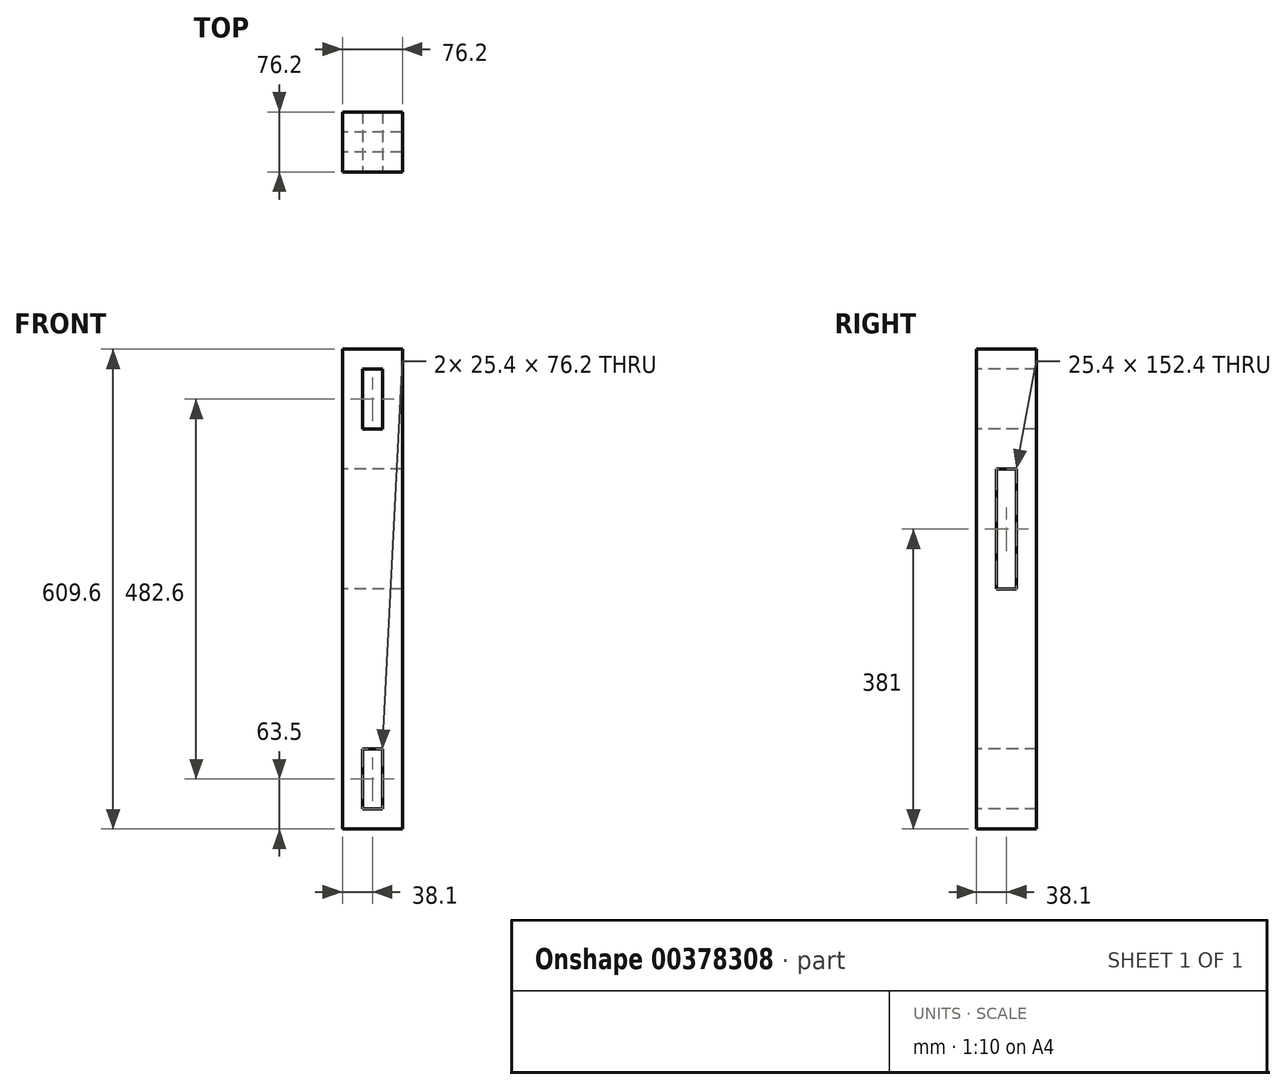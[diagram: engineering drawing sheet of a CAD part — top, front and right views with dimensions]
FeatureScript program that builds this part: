
annotation { "Feature Type Name" : "Feature", "Feature Type Description" : "" }
export const myFeature = defineFeature(function(context is Context, id is Id, definition is map)
    precondition{}
    {
        {
            var Q0;
            Q0=qCreatedBy(makeId("Right.planeOp"),FACE);
            var sketch = newSketch(context, id + "F0", { "sketchPlane" : qUnion([Q0])});
            skLineSegment(sketch, "E0.bottom", {"start": v(-12.7, -88.9) * mm, "end": v(12.7, -88.9) * mm});
            skLineSegment(sketch, "E0.top", {"start": v(-12.7, -241.3) * mm, "end": v(12.7, -241.3) * mm});
            skLineSegment(sketch, "E0.left", {"start": v(-12.7, -88.9) * mm, "end": v(-12.7, -241.3) * mm});
            skLineSegment(sketch, "E0.right", {"start": v(12.7, -88.9) * mm, "end": v(12.7, -241.3) * mm});
            skLineSegment(sketch, "E1.bottom", {"start": v(-38.1, 63.5) * mm, "end": v(38.1, 63.5) * mm});
            skLineSegment(sketch, "E1.top", {"start": v(-38.1, -546.1) * mm, "end": v(38.1, -546.1) * mm});
            skLineSegment(sketch, "E1.left", {"start": v(-38.1, 63.5) * mm, "end": v(-38.1, -546.1) * mm});
            skLineSegment(sketch, "E1.right", {"start": v(38.1, 63.5) * mm, "end": v(38.1, -546.1) * mm});
            skSolve(sketch);
        }
        {
            var Q0;
            Q0 = qSketchRegion(id + "F0", true);
            extrude(context, id + "F1", {"entities" : qUnion([Q0]), "depth" : 38.1 * mm, "hasSecondDirection" : true, "secondDirectionOppositeDirection" : true, "secondDirectionDepth" : 38.1 * mm});
        }
        {
            var Q0;
            Q0=makeQuery(id+"F1.opExtrude","SWEPT_FACE",FACE,{"disambiguationData":[OSD([sQuery(id+"F0.wireOp",EDGE,"E1.left")])]});
            var sketch = newSketch(context, id + "F2", { "sketchPlane" : qUnion([Q0])});
            skLineSegment(sketch, "E2.bottom", {"start": v(-12.7, 38.1) * mm, "end": v(12.7, 38.1) * mm});
            skLineSegment(sketch, "E2.top", {"start": v(-12.7, -38.1) * mm, "end": v(12.7, -38.1) * mm});
            skLineSegment(sketch, "E2.left", {"start": v(-12.7, 38.1) * mm, "end": v(-12.7, -38.1) * mm});
            skLineSegment(sketch, "E2.right", {"start": v(12.7, 38.1) * mm, "end": v(12.7, -38.1) * mm});
            skLineSegment(sketch, "E3.bottom", {"start": v(-12.7, -444.5) * mm, "end": v(12.7, -444.5) * mm});
            skLineSegment(sketch, "E3.top", {"start": v(-12.7, -520.7) * mm, "end": v(12.7, -520.7) * mm});
            skLineSegment(sketch, "E3.left", {"start": v(-12.7, -444.5) * mm, "end": v(-12.7, -520.7) * mm});
            skLineSegment(sketch, "E3.right", {"start": v(12.7, -444.5) * mm, "end": v(12.7, -520.7) * mm});
            skSolve(sketch);
        }
        {
            var Q0;
            Q0=makeQuery(id+"F2.imprint","IMPRINT",FACE,{"disambiguationData":[TD([[makeQuery(id+"F2.imprint","IMPRINT",EDGE,{"derivedFrom":sQuery(id+"F2.wireOp",EDGE,"E2.bottom")}),-1.0]])]});
            var Q1;
            Q1=makeQuery(id+"F2.imprint","IMPRINT",FACE,{"disambiguationData":[TD([[makeQuery(id+"F2.imprint","IMPRINT",EDGE,{"derivedFrom":sQuery(id+"F2.wireOp",EDGE,"E3.bottom")}),-1.0]])]});
            extrude(context, id + "F3", {"entities" : qUnion([Q0, Q1]), "operationType" : NewBodyOperationType.REMOVE, "oppositeDirection" : true, "depth" : 101.6 * mm});
        }
    });
